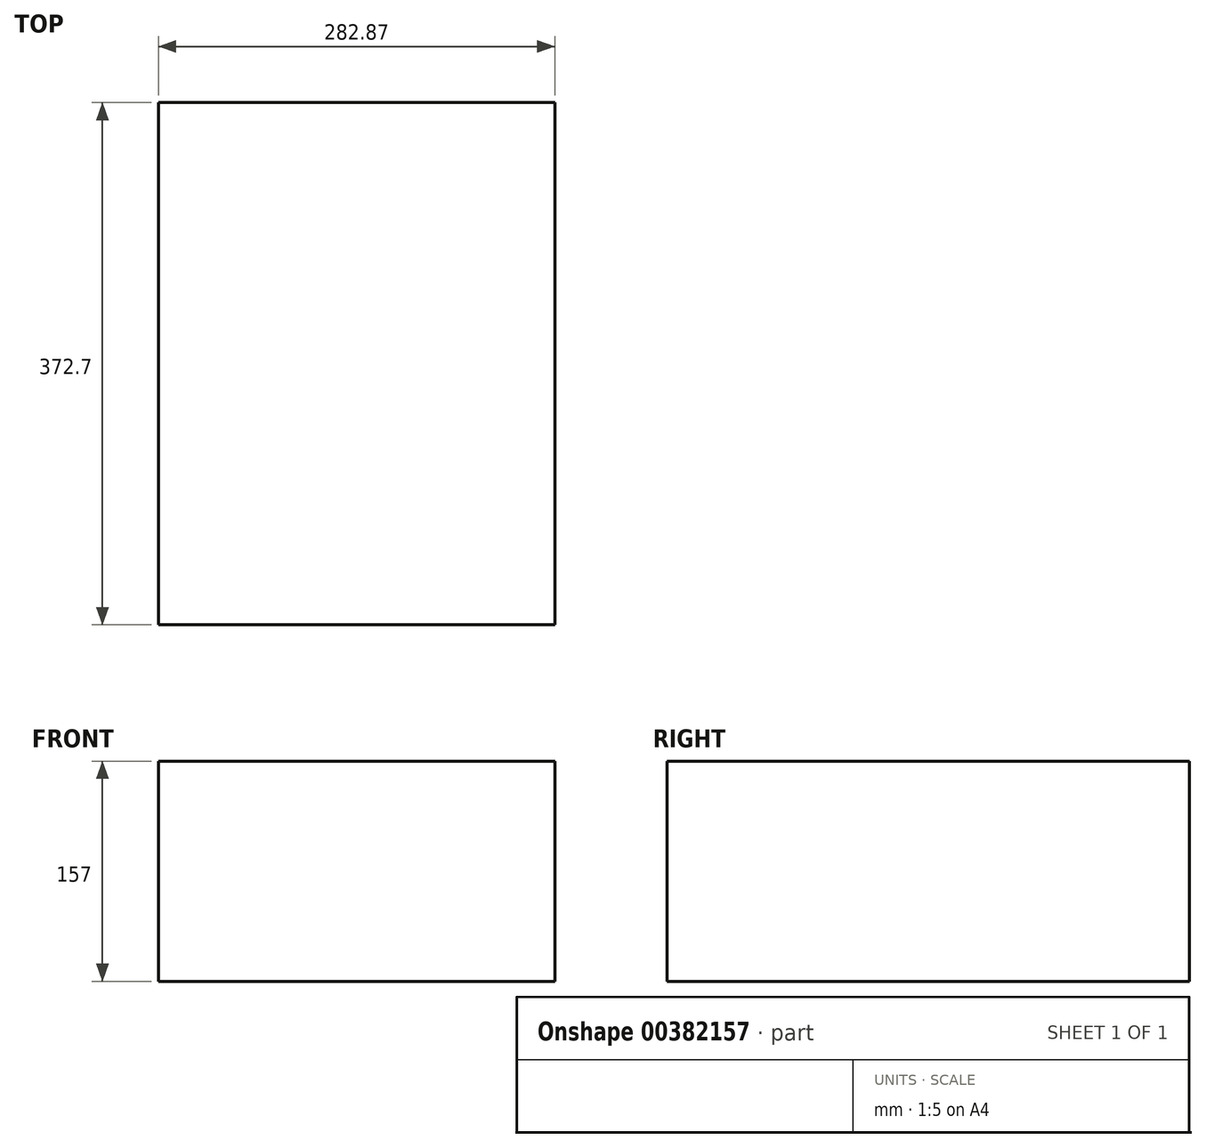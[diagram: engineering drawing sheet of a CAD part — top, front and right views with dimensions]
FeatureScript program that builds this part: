
annotation { "Feature Type Name" : "Feature", "Feature Type Description" : "" }
export const myFeature = defineFeature(function(context is Context, id is Id, definition is map)
    precondition{}
    {
        {
            var Q0;
            Q0=qCreatedBy(makeId("Top.planeOp"),FACE);
            var sketch = newSketch(context, id + "F0", { "sketchPlane" : qUnion([Q0])});
            skLineSegment(sketch, "E0.bottom", {"start": v(-148.18, -162.95) * mm, "end": v(-431.05, -162.95) * mm});
            skLineSegment(sketch, "E0.top", {"start": v(-148.18, 209.75) * mm, "end": v(-431.05, 209.75) * mm});
            skLineSegment(sketch, "E0.left", {"start": v(-148.18, -162.95) * mm, "end": v(-148.18, 209.75) * mm});
            skLineSegment(sketch, "E0.right", {"start": v(-431.05, -162.95) * mm, "end": v(-431.05, 209.75) * mm});
            skSolve(sketch);
        }
        {
            var Q0;
            Q0=makeQuery(id+"F0.imprint","IMPRINT",FACE,{"disambiguationData":[TD([[makeQuery(id+"F0.imprint","IMPRINT",EDGE,{"derivedFrom":sQuery(id+"F0.wireOp",EDGE,"E0.bottom")}),-1.0]])]});
            extrude(context, id + "F1", {"entities" : qUnion([Q0]), "depth" : 157 * mm});
        }
    });
